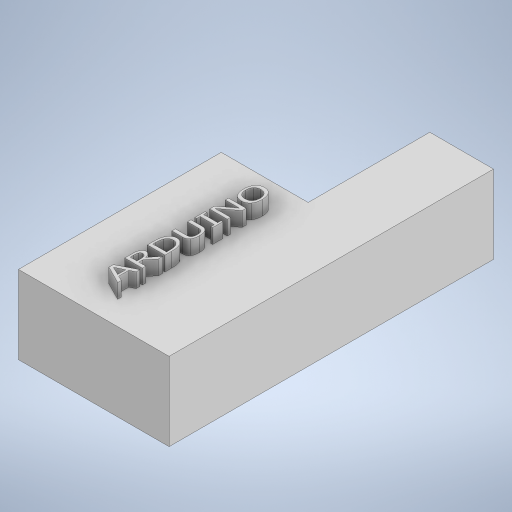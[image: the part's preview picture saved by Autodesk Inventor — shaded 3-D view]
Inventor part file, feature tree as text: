
AUTODESK INVENTOR PART (.ipt)
format: ipt  version: 2023 (Build 270158000, 158)  size: 345,600 bytes
history: native  units: mm
features: extrude x2, sketch x2, other x1
ambient origin geometry x8: Origin, YZ Plane, XZ Plane, XY Plane, X Axis, Y Axis, Z Axis, Center Point
bodies: Body1 (feature_tree)
feature tree (5):
  other  "Sólido1"
  extrude  "Extrusión1"  Depth=70.0mm
  extrude  "Extrusión2"  Depth=42.0mm
  sketch  "Boceto1"  dims[d0=52.0mm d1=70.0mm]
  sketch  "Boceto2"  dims[d2=22.0mm d3=42.0mm d4=27.0mm d5=0.0mm d6=5.0mm d7=0.0mm]
